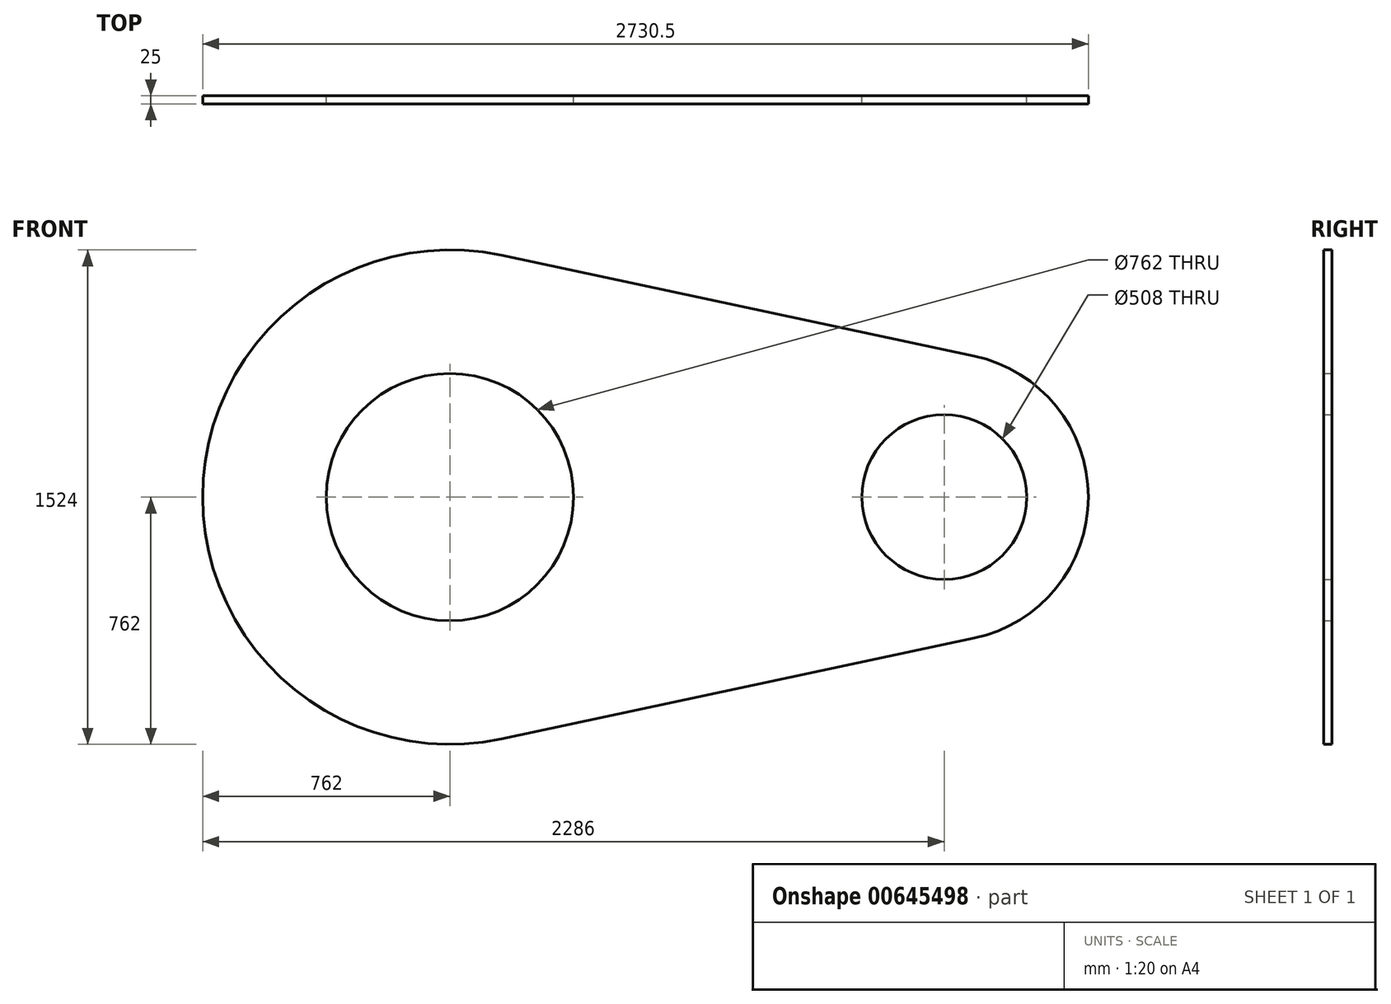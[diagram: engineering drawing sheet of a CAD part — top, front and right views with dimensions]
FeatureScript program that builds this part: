
annotation { "Feature Type Name" : "Feature", "Feature Type Description" : "" }
export const myFeature = defineFeature(function(context is Context, id is Id, definition is map)
    precondition{}
    {
        {
            var Q0;
            Q0=qCreatedBy(makeId("Front.planeOp"),FACE);
            var sketch = newSketch(context, id + "F0", { "sketchPlane" : qUnion([Q0])});
            skCircle(sketch, "E0", {"center": v(0, 0) * mm, "radius": 762 * mm});
            skCircle(sketch, "E1", {"center": v(1524, 0) * mm, "radius": 444.5 * mm});
            skLineSegment(sketch, "E2", {"start": v(158.75, 745.28) * mm, "end": v(1616.6, 434.75) * mm});
            skLineSegment(sketch, "E3", {"start": v(158.75, -745.28) * mm, "end": v(1616.6, -434.75) * mm});
            skCircle(sketch, "E4", {"center": v(0, 0) * mm, "radius": 381 * mm});
            skCircle(sketch, "E5", {"center": v(1524, 0) * mm, "radius": 254 * mm});
            skSolve(sketch);
        }
        {
            var Q0;
            Q0 = qSketchRegion(id + "F0", true);
            extrude(context, id + "F1", {"entities" : qUnion([Q0]), "depth" : 25 * mm, "offsetDistance" : 25.4 * mm});
        }
    });
